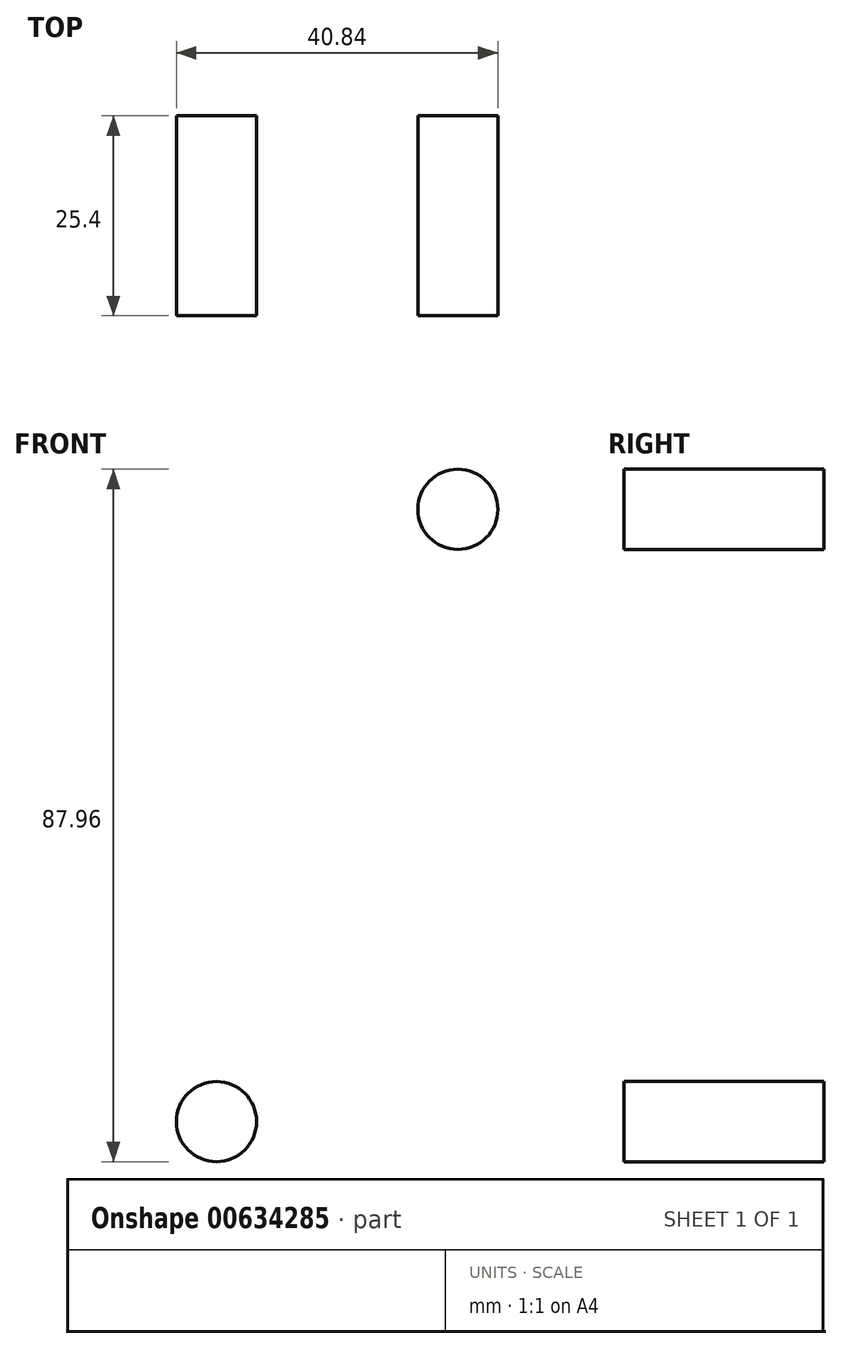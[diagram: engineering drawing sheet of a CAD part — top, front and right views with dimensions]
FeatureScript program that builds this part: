
annotation { "Feature Type Name" : "Feature", "Feature Type Description" : "" }
export const myFeature = defineFeature(function(context is Context, id is Id, definition is map)
    precondition{}
    {
        {
            var Q0;
            Q0=qCreatedBy(makeId("Front.planeOp"),FACE);
            var sketch = newSketch(context, id + "F0", { "sketchPlane" : qUnion([Q0])});
            skLineSegment(sketch, "E0.bottom", {"start": v(-25.4, 50.8) * mm, "end": v(25.4, 50.8) * mm});
            skLineSegment(sketch, "E0.top", {"start": v(-25.4, -50.8) * mm, "end": v(25.4, -50.8) * mm});
            skLineSegment(sketch, "E0.left", {"start": v(-25.4, 50.8) * mm, "end": v(-25.4, -50.8) * mm});
            skLineSegment(sketch, "E0.right", {"start": v(25.4, 50.8) * mm, "end": v(25.4, -50.8) * mm});
            skPoint(sketch, "E0.middle", {"position": v(0, 0) * mm});
            skCircle(sketch, "E1", {"center": v(0, -24.38) * mm, "radius": 7.62 * mm});
            skCircle(sketch, "E2.MirrorC", {"center": v(0, 24.38) * mm, "radius": 7.62 * mm});
            skSolve(sketch);
        }
        {
            var Q0;
            Q0=makeQuery(id+"F0.imprint","IMPRINT",FACE,{"disambiguationData":[TD([[makeQuery(id+"F0.imprint","IMPRINT",EDGE,{"derivedFrom":sQuery(id+"F0.wireOp",EDGE,"E0.bottom")}),-1.0]])]});
            extrude(context, id + "F1", {"entities" : qUnion([Q0]), "endBound" : BoundingType.SYMMETRIC, "depth" : 25.4 * mm, "offsetDistance" : 25.4 * mm});
        }
        {
            var Q0;
            Q0=makeQuery(id+"F1.opExtrude","SWEPT_EDGE",EDGE,{"disambiguationData":[OSD([sQuery(id+"F0.wireOp",EDGE,"E0.bottom"),sQuery(id+"F0.wireOp",EDGE,"E0.right")])]});
            var Q1;
            Q1=makeQuery(id+"F1.opExtrude","SWEPT_EDGE",EDGE,{"disambiguationData":[OSD([sQuery(id+"F0.wireOp",EDGE,"E0.bottom"),sQuery(id+"F0.wireOp",EDGE,"E0.left")])]});
            var Q2;
            Q2=makeQuery(id+"F1.opExtrude","SWEPT_EDGE",EDGE,{"disambiguationData":[OSD([sQuery(id+"F0.wireOp",EDGE,"E0.top"),sQuery(id+"F0.wireOp",EDGE,"E0.right")])]});
            var Q3;
            Q3=makeQuery(id+"F1.opExtrude","SWEPT_EDGE",EDGE,{"disambiguationData":[OSD([sQuery(id+"F0.wireOp",EDGE,"E0.top"),sQuery(id+"F0.wireOp",EDGE,"E0.left")])]});
            fillet(context, id + "F2", {"entities" : qUnion([Q0, Q1, Q2, Q3]), "radius" : 5.08 * mm, "tangentPropagation" : true, "allowEdgeOverflow" : false});
        }
        {
            var Q0;
            Q0=makeQuery(id+"F1.opExtrude","CAP_FACE",FACE,{"disambiguationData":[OSD([sQuery(id+"F0.wireOp",EDGE,"E0.bottom"),sQuery(id+"F0.wireOp",EDGE,"E0.top"),sQuery(id+"F0.wireOp",EDGE,"E0.left"),sQuery(id+"F0.wireOp",EDGE,"E0.right"),sQuery(id+"F0.wireOp",EDGE,"E1"),sQuery(id+"F0.wireOp",EDGE,"E2.MirrorC")])],"isStart":false});
            var sketch = newSketch(context, id + "F3", { "sketchPlane" : qUnion([Q0])});
            skCircle(sketch, "E3", {"center": v(-15.33, 38.89) * mm, "radius": 5.1 * mm});
            skCircle(sketch, "E4.MirrorC", {"center": v(15.33, 38.89) * mm, "radius": 5.1 * mm});
            skCircle(sketch, "E5.MirrorC", {"center": v(-15.33, -38.89) * mm, "radius": 5.1 * mm});
            skCircle(sketch, "E6.MirrorC", {"center": v(15.33, -38.89) * mm, "radius": 5.1 * mm});
            skSolve(sketch);
        }
        {
            var Q0;
            Q0=makeQuery(id+"F3.imprint","IMPRINT",FACE,{"disambiguationData":[TD([[makeQuery(id+"F3.imprint","IMPRINT",EDGE,{"derivedFrom":sQuery(id+"F3.wireOp",EDGE,"E3")}),1.0]])]});
            var Q1;
            Q1=makeQuery(id+"F3.imprint","IMPRINT",FACE,{"disambiguationData":[TD([[makeQuery(id+"F3.imprint","IMPRINT",EDGE,{"derivedFrom":sQuery(id+"F3.wireOp",EDGE,"E4.MirrorC")}),-1.0]])]});
            var Q2;
            Q2=makeQuery(id+"F3.imprint","IMPRINT",FACE,{"disambiguationData":[TD([[makeQuery(id+"F3.imprint","IMPRINT",EDGE,{"derivedFrom":sQuery(id+"F3.wireOp",EDGE,"E6.MirrorC")}),1.0]])]});
            var Q3;
            Q3=makeQuery(id+"F3.imprint","IMPRINT",FACE,{"disambiguationData":[TD([[makeQuery(id+"F3.imprint","IMPRINT",EDGE,{"derivedFrom":sQuery(id+"F3.wireOp",EDGE,"E5.MirrorC")}),-1.0]])]});
            var Q4;
            Q4=makeQuery(id+"F1.opExtrude","CAP_FACE",FACE,{"disambiguationData":[OSD([sQuery(id+"F0.wireOp",EDGE,"E0.bottom"),sQuery(id+"F0.wireOp",EDGE,"E0.top"),sQuery(id+"F0.wireOp",EDGE,"E0.left"),sQuery(id+"F0.wireOp",EDGE,"E0.right"),sQuery(id+"F0.wireOp",EDGE,"E1"),sQuery(id+"F0.wireOp",EDGE,"E2.MirrorC")])],"isStart":true});
            extrude(context, id + "F4", {"entities" : qUnion([Q0, Q1, Q2, Q3]), "operationType" : NewBodyOperationType.REMOVE, "endBound" : BoundingType.UP_TO_SURFACE, "oppositeDirection" : true, "depth" : 25.4 * mm, "endBoundEntityFace" : qUnion([Q4]), "offsetDistance" : 25.4 * mm});
        }
    });
